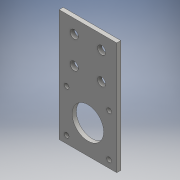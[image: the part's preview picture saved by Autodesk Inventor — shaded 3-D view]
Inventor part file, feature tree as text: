
AUTODESK INVENTOR PART (.ipt)
format: ipt  version: 2016 (Build 200138000, 138)  size: 138,752 bytes
history: native  units: mm
features: extrude x4, sketch x4, projected_geometry x1
ambient origin geometry x8: Origin, YZ Plane, XZ Plane, XY Plane, X Axis, Y Axis, Z Axis, Center Point
bodies: Body1 (feature_tree)
feature tree (9):
  extrude  "拉伸2"  Depth=42.0mm
  extrude  "拉伸6"  Depth=3.0mm
  extrude  "拉伸13"  Depth=15.5mm
  extrude  "拉伸14"  Depth=10.0mm
  sketch  "草图2"  dims[d3=42.0mm d4=42.0mm]
  sketch  "草图7"  dims[d5=3.0mm d6=0.0mm d17=23.0mm]
  sketch  "草图14"  dims[d18=3.5mm d19=15.5mm]
  projected_geometry  "投影回路5"
  sketch  "草图15"  dims[d20=15.5mm d21=15.5mm d22=15.5mm d23=3.0mm d24=0.0mm d49=40.0mm d50=0.0mm d51=6.0mm d52=10.0mm d53=10.0mm d54=6.0mm d55=20.0mm d56=40.0mm d57=0.0mm]
